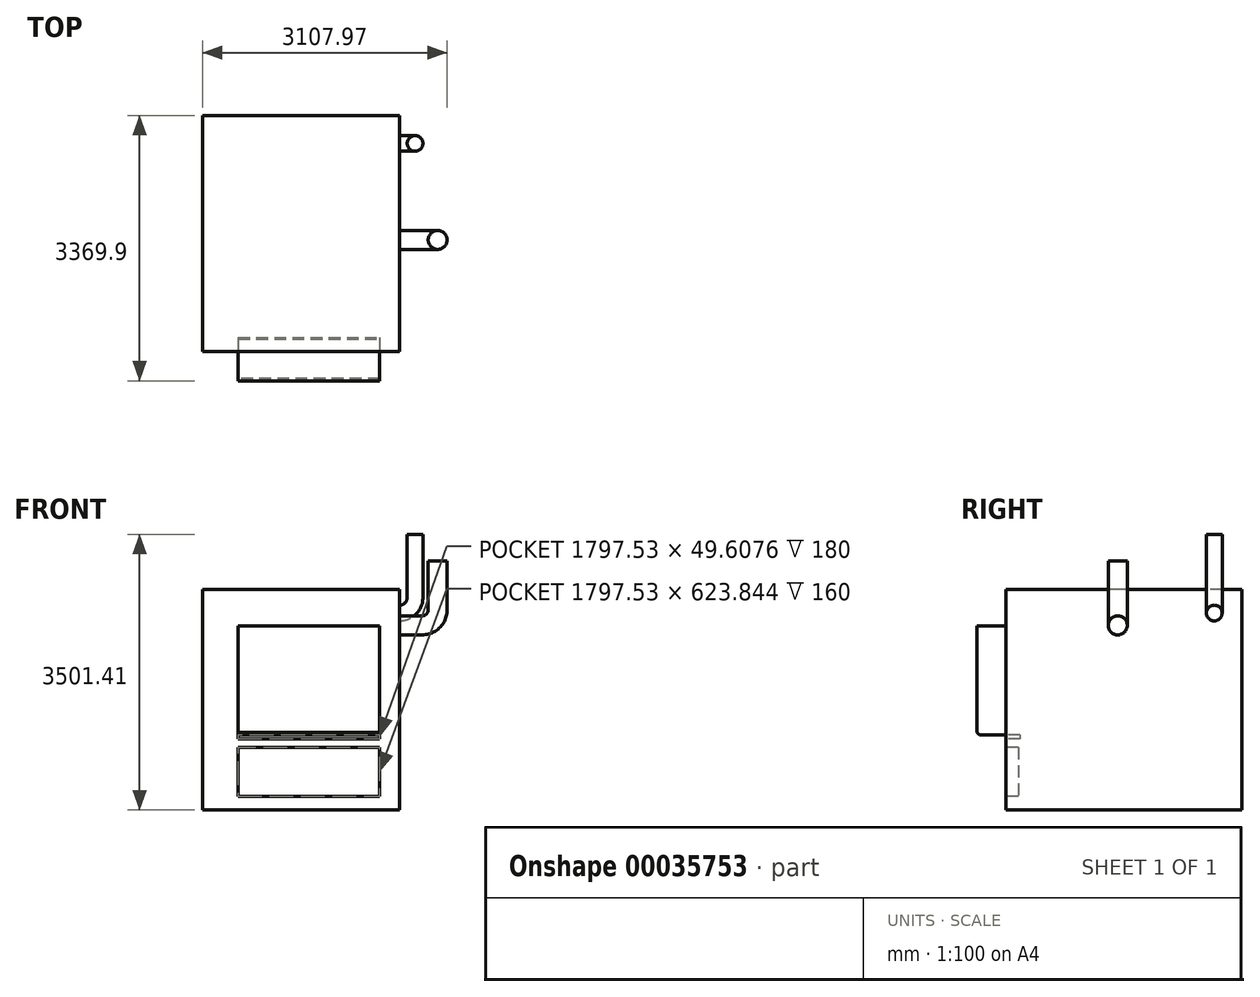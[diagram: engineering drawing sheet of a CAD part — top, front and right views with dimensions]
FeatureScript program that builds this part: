
annotation { "Feature Type Name" : "Feature", "Feature Type Description" : "" }
export const myFeature = defineFeature(function(context is Context, id is Id, definition is map)
    precondition{}
    {
        {
            var Q0;
            Q0=qCreatedBy(makeId("Top.planeOp"),FACE);
            var sketch = newSketch(context, id + "F0", { "sketchPlane" : qUnion([Q0])});
            skLineSegment(sketch, "E0.bottom", {"start": v(6583.8, -5090) * mm, "end": v(9083.8, -5090) * mm});
            skLineSegment(sketch, "E0.top", {"start": v(6583.8, -8090) * mm, "end": v(9083.8, -8090) * mm});
            skLineSegment(sketch, "E0.left", {"start": v(6583.8, -5090) * mm, "end": v(6583.8, -8090) * mm});
            skLineSegment(sketch, "E0.right", {"start": v(9083.8, -5090) * mm, "end": v(9083.8, -8090) * mm});
            skSolve(sketch);
        }
        {
            var Q0;
            Q0=makeQuery(id+"F0.imprint","IMPRINT",FACE,{"disambiguationData":[TD([[makeQuery(id+"F0.imprint","IMPRINT",EDGE,{"derivedFrom":sQuery(id+"F0.wireOp",EDGE,"E0.bottom")}),-1.0]])]});
            extrude(context, id + "F1", {"entities" : qUnion([Q0]), "depth" : 2800 * mm});
        }
        {
            var Q0;
            Q0=makeQuery(id+"F1.opExtrude","SWEPT_FACE",FACE,{"disambiguationData":[OSD([sQuery(id+"F0.wireOp",EDGE,"E0.top")])]});
            var sketch = newSketch(context, id + "F2", { "sketchPlane" : qUnion([Q0])});
            skLineSegment(sketch, "E1.bottom", {"start": v(7036.56, 2337.09) * mm, "end": v(8834.09, 2337.09) * mm});
            skLineSegment(sketch, "E1.top", {"start": v(7036.56, 954.92) * mm, "end": v(8834.09, 954.92) * mm});
            skLineSegment(sketch, "E1.left", {"start": v(7036.56, 2337.09) * mm, "end": v(7036.56, 954.92) * mm});
            skLineSegment(sketch, "E1.right", {"start": v(8834.09, 2337.09) * mm, "end": v(8834.09, 954.92) * mm});
            skSolve(sketch);
        }
        {
            var Q0;
            Q0=makeQuery(id+"F2.imprint","IMPRINT",FACE,{"disambiguationData":[TD([[makeQuery(id+"F2.imprint","IMPRINT",EDGE,{"derivedFrom":sQuery(id+"F2.wireOp",EDGE,"E1.bottom")}),-1.0]])]});
            extrude(context, id + "F3", {"entities" : qUnion([Q0]), "operationType" : NewBodyOperationType.ADD, "depth" : 369.9 * mm});
        }
        {
            var Q0;
            Q0=makeQuery(id+"F1.opExtrude","SWEPT_FACE",FACE,{"disambiguationData":[OSD([sQuery(id+"F0.wireOp",EDGE,"E0.top")])]});
            var sketch = newSketch(context, id + "F4", { "sketchPlane" : qUnion([Q0])});
            skLineSegment(sketch, "E2.bottom", {"start": v(7036.56, 954.92) * mm, "end": v(8834.09, 954.92) * mm});
            skLineSegment(sketch, "E2.top", {"start": v(7036.56, 905.3) * mm, "end": v(8834.09, 905.3) * mm});
            skLineSegment(sketch, "E2.left", {"start": v(7036.56, 954.92) * mm, "end": v(7036.56, 905.3) * mm});
            skLineSegment(sketch, "E2.right", {"start": v(8834.09, 954.92) * mm, "end": v(8834.09, 905.3) * mm});
            skSolve(sketch);
        }
        {
            var Q0;
            Q0=makeQuery(id+"F4.imprint","IMPRINT",FACE,{"disambiguationData":[TD([[makeQuery(id+"F4.imprint","IMPRINT",EDGE,{"derivedFrom":sQuery(id+"F4.wireOp",EDGE,"E2.bottom")}),-1.0]])]});
            extrude(context, id + "F5", {"entities" : qUnion([Q0]), "operationType" : NewBodyOperationType.REMOVE, "oppositeDirection" : true, "depth" : 180 * mm});
        }
        {
            var Q0;
            Q0=makeQuery(id+"F1.opExtrude","SWEPT_FACE",FACE,{"disambiguationData":[OSD([sQuery(id+"F0.wireOp",EDGE,"E0.top")])]});
            var sketch = newSketch(context, id + "F6", { "sketchPlane" : qUnion([Q0])});
            skLineSegment(sketch, "E3.bottom", {"start": v(7036.56, 794.82) * mm, "end": v(8834.09, 794.82) * mm});
            skLineSegment(sketch, "E3.top", {"start": v(7036.56, 170.97) * mm, "end": v(8834.09, 170.97) * mm});
            skLineSegment(sketch, "E3.left", {"start": v(7036.56, 794.82) * mm, "end": v(7036.56, 170.97) * mm});
            skLineSegment(sketch, "E3.right", {"start": v(8834.09, 794.82) * mm, "end": v(8834.09, 170.97) * mm});
            skSolve(sketch);
        }
        {
            var Q0;
            Q0=makeQuery(id+"F6.imprint","IMPRINT",FACE,{"disambiguationData":[TD([[makeQuery(id+"F6.imprint","IMPRINT",EDGE,{"derivedFrom":sQuery(id+"F6.wireOp",EDGE,"E3.bottom")}),-1.0]])]});
            extrude(context, id + "F7", {"entities" : qUnion([Q0]), "operationType" : NewBodyOperationType.REMOVE, "oppositeDirection" : true, "depth" : 160 * mm});
        }
        {
            var Q0;
            Q0=makeQuery(id+"F1.opExtrude","SWEPT_FACE",FACE,{"disambiguationData":[OSD([sQuery(id+"F0.wireOp",EDGE,"E0.right")])]});
            var sketch = newSketch(context, id + "F8", { "sketchPlane" : qUnion([Q0])});
            skCircle(sketch, "E4", {"center": v(-5443.78, 2501.41) * mm, "radius": 100 * mm});
            skSolve(sketch);
        }
        {
            var Q0;
            Q0=makeQuery(id+"F1.opExtrude","SWEPT_FACE",FACE,{"disambiguationData":[OSD([sQuery(id+"F0.wireOp",EDGE,"E0.top")])]});
            var Q1;
            Q1=sQuery(id+"F8.wireOp",VERTEX,"E4.center");
            cPlane(context, id + "F9", {"entities" : qUnion([Q0, Q1]), "cplaneType" : CPlaneType.PLANE_POINT, "offset" : 150 * mm, "width" : 150 * mm, "height" : 150 * mm});
        }
        {
            var Q0;
            Q0=qCreatedBy(id+"F9.planeOp",FACE);
            var sketch = newSketch(context, id + "F10", { "sketchPlane" : qUnion([Q0])});
            skLineSegment(sketch, "E5.0", {"start": v(9083.8, 2601.41) * mm, "end": v(9083.8, 2401.41) * mm});
            skLineSegment(sketch, "E6", {"start": v(9083.8, 2501.41) * mm, "end": v(9083.8, 2501.41) * mm});
            skLineSegment(sketch, "E7", {"start": v(9283.8, 2701.41) * mm, "end": v(9283.8, 3501.41) * mm});
            skPoint(sketch, "E8.visualSharp", {"position": v(9283.8, 2501.41) * mm});
            skArc(sketch, "E8.filletArc", {"start": v(9083.8, 2501.41) * mm, "mid": v(9225.22, 2560) * mm, "end": v(9283.8, 2701.41) * mm});
            skSolve(sketch);
        }
        {
            var Q0;
            Q0=makeQuery(id+"F8.imprint","IMPRINT",FACE,{"disambiguationData":[TD([[makeQuery(id+"F8.imprint","IMPRINT",EDGE,{"derivedFrom":sQuery(id+"F8.wireOp",EDGE,"E4")}),1.0]])]});
            var Q1;
            Q1=sQuery(id+"F10.wireOp",EDGE,"E8.filletArc");
            var Q2;
            Q2=sQuery(id+"F10.wireOp",EDGE,"E7");
            sweep(context, id + "F11", {"operationType" : NewBodyOperationType.ADD, "profiles" : qUnion([Q0]), "path" : qUnion([Q1, Q2])});
        }
        {
            var Q0;
            Q0=makeQuery(id+"F3.opExtrude","CAP_EDGE",EDGE,{"disambiguationData":[OSD([sQuery(id+"F2.wireOp",EDGE,"E1.top")])],"isStart":false});
            chamfer(context, id + "F12", {"entities" : qUnion([Q0]), "width" : 30 * mm, "tangentPropagation" : true});
        }
        {
            var Q0;
            Q0=makeQuery(id+"F1.opExtrude","SWEPT_FACE",FACE,{"disambiguationData":[OSD([sQuery(id+"F0.wireOp",EDGE,"E0.right")])]});
            var sketch = newSketch(context, id + "F13", { "sketchPlane" : qUnion([Q0])});
            skCircle(sketch, "E9", {"center": v(-6669.53, 2344.4) * mm, "radius": 120.71 * mm});
            skSolve(sketch);
        }
        {
            var Q0;
            Q0=sQuery(id+"F13.wireOp",VERTEX,"E9.center");
            var Q1;
            Q1=qCreatedBy(makeId("Front.planeOp"),FACE);
            cPlane(context, id + "F14", {"entities" : qUnion([Q0, Q1]), "cplaneType" : CPlaneType.PLANE_POINT, "offset" : 25 * mm, "width" : 150 * mm, "height" : 150 * mm});
        }
        {
            var Q0;
            Q0=qCreatedBy(id+"F14.planeOp",FACE);
            var sketch = newSketch(context, id + "F15", { "sketchPlane" : qUnion([Q0])});
            skLineSegment(sketch, "E10.0", {"start": v(9083.8, 2465.11) * mm, "end": v(9083.8, 2223.69) * mm});
            skLineSegment(sketch, "E11", {"start": v(9083.8, 2344.4) * mm, "end": v(9371.06, 2344.4) * mm});
            skLineSegment(sketch, "E12", {"start": v(9571.06, 2544.4) * mm, "end": v(9571.06, 3160.71) * mm});
            skPoint(sketch, "E13.visualSharp", {"position": v(9571.06, 2344.4) * mm});
            skArc(sketch, "E13.filletArc", {"start": v(9371.06, 2344.4) * mm, "mid": v(9512.48, 2402.98) * mm, "end": v(9571.06, 2544.4) * mm});
            skSolve(sketch);
        }
        {
            var Q0;
            Q0=makeQuery(id+"F13.imprint","IMPRINT",FACE,{"disambiguationData":[TD([[makeQuery(id+"F13.imprint","IMPRINT",EDGE,{"derivedFrom":sQuery(id+"F13.wireOp",EDGE,"E9")}),1.0]])]});
            var Q1;
            Q1=sQuery(id+"F15.wireOp",EDGE,"E11");
            var Q2;
            Q2=sQuery(id+"F15.wireOp",EDGE,"E13.filletArc");
            var Q3;
            Q3=sQuery(id+"F15.wireOp",EDGE,"E12");
            sweep(context, id + "F16", {"profiles" : qUnion([Q0]), "path" : qUnion([Q1, Q2, Q3])});
        }
    });
